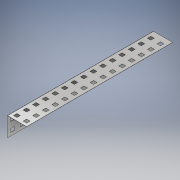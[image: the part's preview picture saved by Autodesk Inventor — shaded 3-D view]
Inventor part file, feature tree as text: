
AUTODESK INVENTOR PART (.ipt)
format: ipt  version: 2018 (Build 220112000, 112)  size: 366,592 bytes
history: native  units: in
note: dims shown in document units (in); Inventor stores cm internally (conversion verified against a paired STEP export)
features: sketch x4, extrude x4
ambient origin geometry x8: Origin, YZ Plane, XZ Plane, XY Plane, X Axis, Y Axis, Z Axis, Center Point
bodies: Solid1 (feature_tree), Solid2 (feature_tree)
feature tree (8):
  sketch  "Sketch1"  dims[d0=0.984in d1=7.48in]
  extrude  "Extrusion1"  Depth=7.48in
  extrude  "Extrusion2"  Depth=7.48in
  extrude  "Extrusion3"  Depth=0.01in TaperAngle=0.0deg
  extrude  "Extrusion4"  Depth=0.18in
  sketch  "Sketch2"  dims[d2=0.984in d3=7.48in]
  sketch  "Sketch3"  dims[d4=0.01in d5=0.0in d6=0.01in d7=0.0in]
  sketch  "Sketch4"  dims[d8=0.18in d9=0.18in d10=0.154in d11=0.3937in d13=1.0in d14=5.9055in d16=0.49in d18=0.01in d19=0.0in d20=0.18in d21=0.18in d22=0.3937in d24=1.0in d25=5.9055in d27=0.49in d29=0.01in d30=0.0in]
